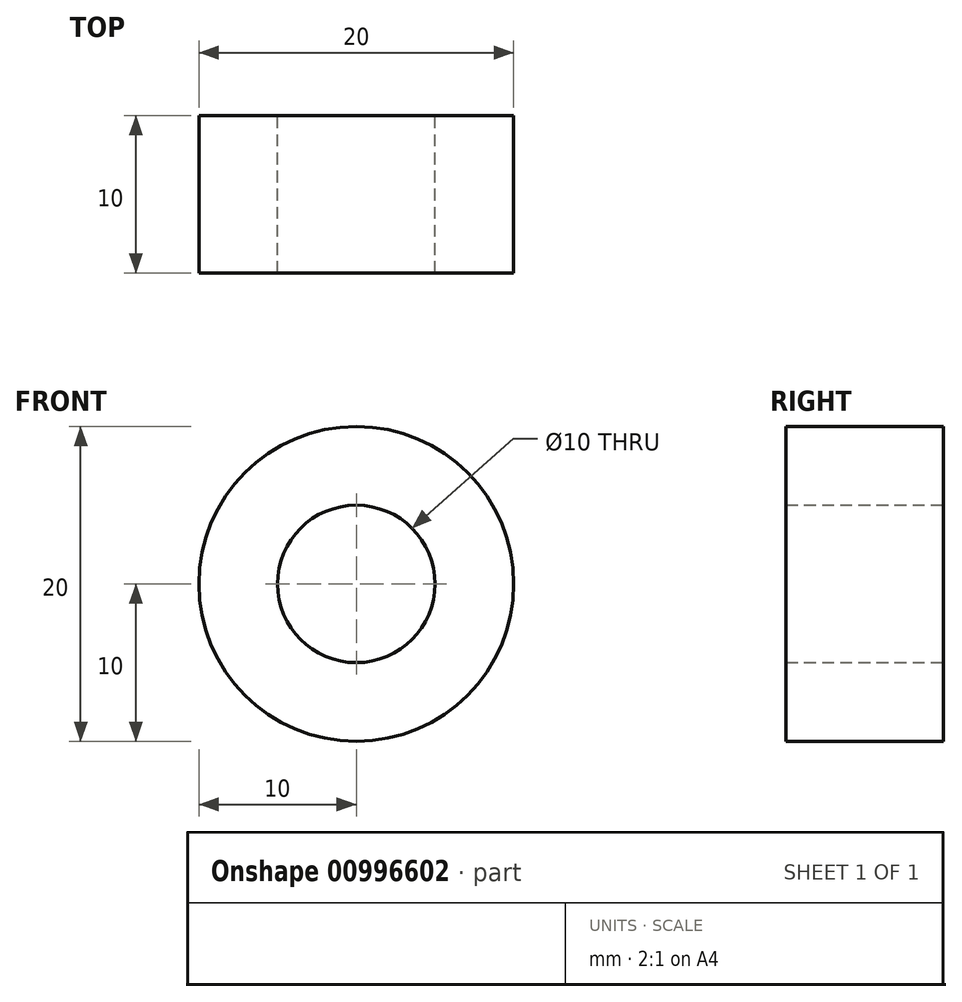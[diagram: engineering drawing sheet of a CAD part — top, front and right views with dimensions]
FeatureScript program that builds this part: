
annotation { "Feature Type Name" : "Feature", "Feature Type Description" : "" }
export const myFeature = defineFeature(function(context is Context, id is Id, definition is map)
    precondition{}
    {
        {
            var Q0;
            Q0=qCreatedBy(makeId("Front.planeOp"),FACE);
            var sketch = newSketch(context, id + "F0", { "sketchPlane" : qUnion([Q0])});
            skCircle(sketch, "E0", {"center": v(0, 0) * mm, "radius": 10 * mm});
            skCircle(sketch, "E1", {"center": v(0, 0) * mm, "radius": 5 * mm});
            skSolve(sketch);
        }
        {
            var Q0;
            Q0=makeQuery(id+"F0.imprint","IMPRINT",FACE,{"disambiguationData":[TD([[makeQuery(id+"F0.imprint","IMPRINT",EDGE,{"derivedFrom":sQuery(id+"F0.wireOp",EDGE,"E0")}),1.0]])]});
            extrude(context, id + "F1", {"entities" : qUnion([Q0]), "depth" : 10 * mm, "offsetDistance" : 25 * mm});
        }
    });
